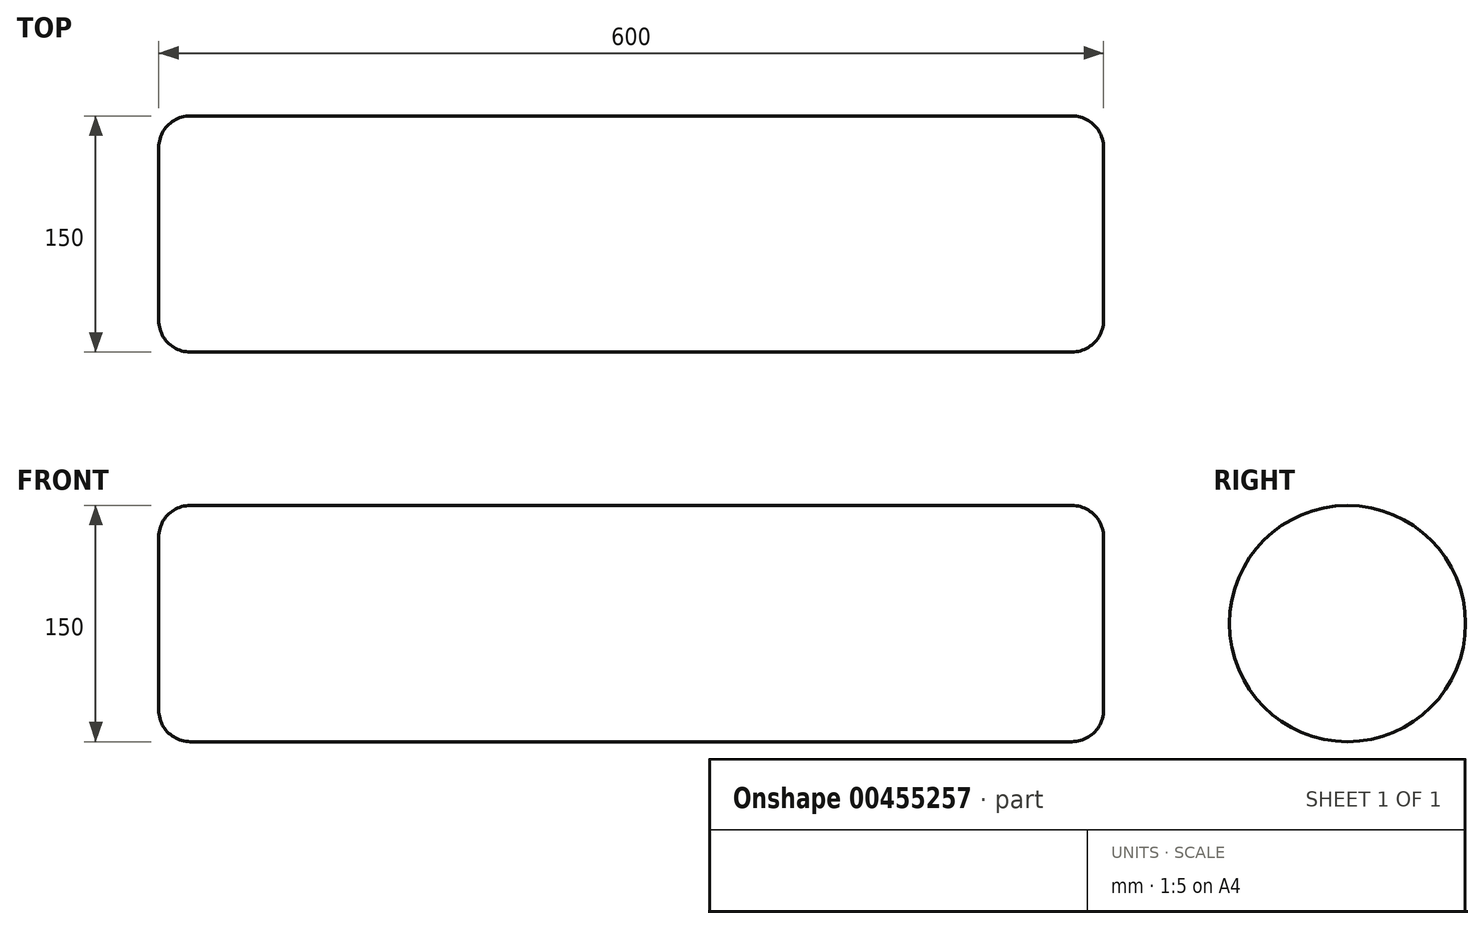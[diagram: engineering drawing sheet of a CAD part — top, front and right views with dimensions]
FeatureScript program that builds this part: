
annotation { "Feature Type Name" : "Feature", "Feature Type Description" : "" }
export const myFeature = defineFeature(function(context is Context, id is Id, definition is map)
    precondition{}
    {
        {
            var Q0;
            Q0=qCreatedBy(makeId("Right.planeOp"),FACE);
            var sketch = newSketch(context, id + "F0", { "sketchPlane" : qUnion([Q0])});
            skCircle(sketch, "E0", {"center": v(0, 0) * mm, "radius": 75 * mm});
            skSolve(sketch);
        }
        {
            var Q0;
            Q0 = qSketchRegion(id + "F0", true);
            extrude(context, id + "F1", {"entities" : qUnion([Q0]), "depth" : 600 * mm, "offsetDistance" : 25 * mm, "symmetric" : true});
        }
        {
            var Q0;
            Q0=makeQuery(id+"F1.opExtrude","SWEPT_FACE",FACE,{"disambiguationData":[OSD([sQuery(id+"F0.wireOp",EDGE,"E0")])]});
            fillet(context, id + "F2", {"entities" : qUnion([Q0]), "radius" : 20 * mm, "tangentPropagation" : true, "allowEdgeOverflow" : false});
        }
    });
